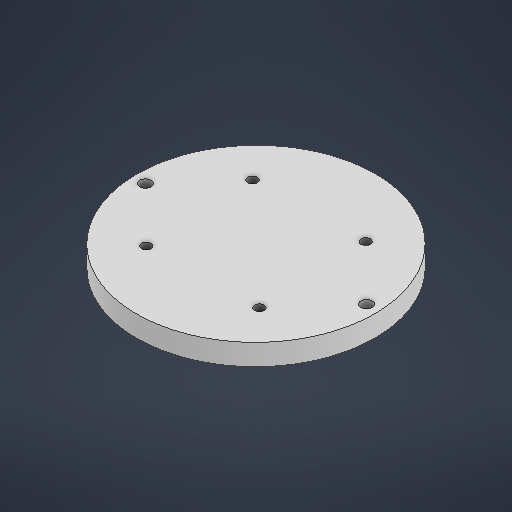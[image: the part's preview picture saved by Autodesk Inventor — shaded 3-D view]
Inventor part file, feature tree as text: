
AUTODESK INVENTOR PART (.ipt)
format: ipt  version: 2025 (Build 290162000, 162)  size: 218,112 bytes
history: native  units: in
note: dims shown in document units (in); Inventor stores cm internally (conversion verified against a paired STEP export)
features: sketch x4, extrude x3, hole x1
ambient origin geometry x8: Origin, YZ Plane, XZ Plane, XY Plane, X Axis, Y Axis, Z Axis, Center Point
bodies: Solid1 (feature_tree)
feature tree (8):
  extrude  "Extrusion1"  Depth=0.5906in TaperAngle=0.0deg
  sketch  "Sketch2"  dims[d5=0.315in d6=0.1772in]
  extrude  "Extrusion2"  Depth=0.315in
  extrude  "Extrusion3"  Depth=0.1772in
  hole  "Hole1"  [1 undecoded]
  sketch  "Sketch1"  dims[d0=6.6732in d1=0.5906in d2=0.0in]
  sketch  "Sketch3"  dims[d7=0.1772in d8=0.0in d9=0.0in d10=0.4724in d11=0.0in d12=1.5748in d13=0.315in d14=1.5748in d16=360.0deg d21=4.3307in d22=4.3307in d23=4.3307in d24=0.315in d25=0.315in d26=0.315in d27=0.315in d28=0.2617in d29=0.4724in d30=0.1575in d31=0.0787in d32=90.0deg d33=0.4724in d34=0.8108in]
  sketch  "Sketch Circular Pattern1"  dims[d3=5.9843in d4=0.315in]
note: 1 required parameter value undecoded (feature->parameter linkage not recoverable at this tier; creation-order binding heuristic only, values carry confidence <= 0.55)
